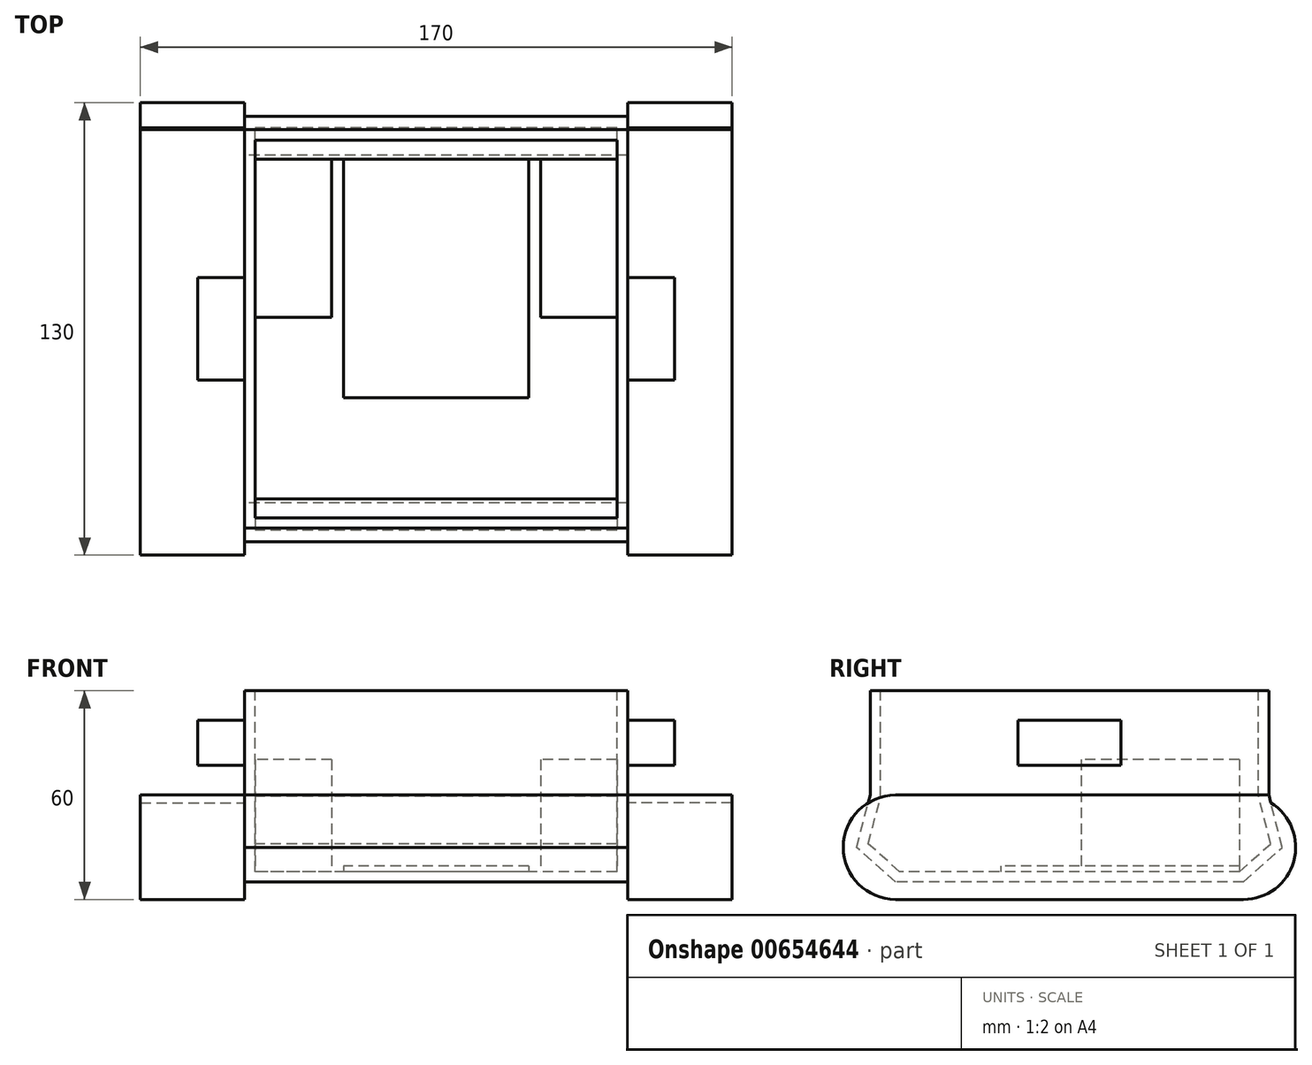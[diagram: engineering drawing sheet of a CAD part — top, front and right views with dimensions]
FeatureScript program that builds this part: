
annotation { "Feature Type Name" : "Feature", "Feature Type Description" : "" }
export const myFeature = defineFeature(function(context is Context, id is Id, definition is map)
    precondition{}
    {
        {
            var Q0;
            Q0=qCreatedBy(makeId("Right.planeOp"),FACE);
            var sketch = newSketch(context, id + "F0", { "sketchPlane" : qUnion([Q0])});
            skLineSegment(sketch, "E0", {"start": v(0, 0) * mm, "end": v(50, 0) * mm, "construction": true});
            skLineSegment(sketch, "E1", {"start": v(0, 0) * mm, "end": v(-50, 0) * mm, "construction": true});
            skCircle(sketch, "E2", {"center": v(50, 0) * mm, "radius": 15 * mm});
            skCircle(sketch, "E3", {"center": v(-50, 0) * mm, "radius": 15 * mm});
            skLineSegment(sketch, "E4", {"start": v(-50, 15) * mm, "end": v(50, 15) * mm});
            skLineSegment(sketch, "E5", {"start": v(50, -15) * mm, "end": v(-50, -15) * mm});
            skLineSegment(sketch, "E6", {"start": v(0, 0) * mm, "end": v(0, -10) * mm, "construction": true});
            skLineSegment(sketch, "E7", {"start": v(0, -10) * mm, "end": v(-50, -10) * mm});
            skLineSegment(sketch, "E8", {"start": v(-50, -10) * mm, "end": v(-61.18, 0) * mm});
            skLineSegment(sketch, "E9", {"start": v(0, -10) * mm, "end": v(50, -10) * mm});
            skLineSegment(sketch, "E10", {"start": v(50, -10) * mm, "end": v(61.18, 0) * mm});
            skLineSegment(sketch, "E11", {"start": v(61.18, 0) * mm, "end": v(57.28, 15) * mm});
            skLineSegment(sketch, "E12", {"start": v(-61.18, 0) * mm, "end": v(-57.28, 15) * mm});
            skLineSegment(sketch, "E13", {"start": v(-57.28, 15) * mm, "end": v(-50, 15) * mm});
            skLineSegment(sketch, "E14", {"start": v(57.28, 15) * mm, "end": v(50, 15) * mm});
            skLineSegment(sketch, "E15.bottom", {"start": v(-57.28, 15) * mm, "end": v(57.28, 15) * mm});
            skLineSegment(sketch, "E15.top", {"start": v(-57.28, 45) * mm, "end": v(57.28, 45) * mm});
            skLineSegment(sketch, "E15.left", {"start": v(-57.28, 15) * mm, "end": v(-57.28, 45) * mm});
            skLineSegment(sketch, "E15.right", {"start": v(57.28, 15) * mm, "end": v(57.28, 45) * mm});
            skLineSegment(sketch, "E16.bottom", {"start": v(14.75, 23.5) * mm, "end": v(-14.75, 23.5) * mm});
            skLineSegment(sketch, "E16.top", {"start": v(14.75, 36.5) * mm, "end": v(-14.75, 36.5) * mm});
            skLineSegment(sketch, "E16.left", {"start": v(14.75, 23.5) * mm, "end": v(14.75, 36.5) * mm});
            skLineSegment(sketch, "E16.right", {"start": v(-14.75, 23.5) * mm, "end": v(-14.75, 36.5) * mm});
            skPoint(sketch, "E16.middle", {"position": v(0, 30) * mm});
            skPoint(sketch, "E16.middle.positionSnap0", {"position": v(-57.28, 30) * mm});
            skPoint(sketch, "E16.centerSnap0", {"position": v(-57.28, 30) * mm});
            skSolve(sketch);
        }
        {
            var Q0;
            {var subQ5=sQuery(id+"F0.wireOp",EDGE,"E4");Q0=makeQuery(id+"F0.imprint","IMPRINT",FACE,{"disambiguationData":[TD([[makeQuery(id+"F0.imprint","IMPRINT",EDGE,{"derivedFrom":subQ5}),-1.0]])]});}
            var Q1;
            {var subQ4=sQuery(id+"F0.wireOp",EDGE,"E10");Q1=makeQuery(id+"F0.imprint","IMPRINT",FACE,{"disambiguationData":[TD([[makeQuery(id+"F0.imprint","IMPRINT",EDGE,{"derivedFrom":subQ4}),1.0]])]});}
            var Q2;
            {var subQ4=sQuery(id+"F0.wireOp",EDGE,"E8");Q2=makeQuery(id+"F0.imprint","IMPRINT",FACE,{"disambiguationData":[TD([[makeQuery(id+"F0.imprint","IMPRINT",EDGE,{"derivedFrom":subQ4}),-1.0]])]});}
            var Q3;
            {var subQ0=sQuery(id+"F0.wireOp",EDGE,"E13");Q3=makeQuery(id+"F0.imprint","IMPRINT",FACE,{"disambiguationData":[TD([[makeQuery(id+"F0.imprint","IMPRINT",EDGE,{"derivedFrom":subQ0}),-1.0]])]});}
            var Q4;
            {var subQ0=sQuery(id+"F0.wireOp",EDGE,"E14");Q4=makeQuery(id+"F0.imprint","IMPRINT",FACE,{"disambiguationData":[TD([[makeQuery(id+"F0.imprint","IMPRINT",EDGE,{"derivedFrom":subQ0}),1.0]])]});}
            var Q5;
            Q5=makeQuery(id+"F0.imprint","IMPRINT",FACE,{"disambiguationData":[TD([[makeQuery(id+"F0.imprint","IMPRINT",EDGE,{"derivedFrom":sQuery(id+"F0.wireOp",EDGE,"E15.top")}),-1.0]])]});
            var Q6;
            {var subQ0=sQuery(id+"F0.wireOp",EDGE,"E11");var subQ1=sQuery(id+"F0.wireOp",EDGE,"E2");var subQ2=makeQuery(id+"F0.imprint","INTERSECT",VERTEX,{"derivedFrom":[subQ1,subQ0]});Q6=makeQuery(id+"F0.imprint","IMPRINT",FACE,{"disambiguationData":[TD([[makeQuery(id+"F0.imprint","IMPRINT",EDGE,{"disambiguationData":[TD([[subQ2,-1.0]])],"derivedFrom":subQ1}),-1.0]])]});}
            var Q7;
            {var subQ0=sQuery(id+"F0.wireOp",EDGE,"E12");var subQ1=sQuery(id+"F0.wireOp",EDGE,"E3");var subQ2=makeQuery(id+"F0.imprint","INTERSECT",VERTEX,{"derivedFrom":[subQ1,subQ0]});Q7=makeQuery(id+"F0.imprint","IMPRINT",FACE,{"disambiguationData":[TD([[makeQuery(id+"F0.imprint","IMPRINT",EDGE,{"disambiguationData":[TD([[subQ2,1.0]])],"derivedFrom":subQ1}),-1.0]])]});}
            var Q8;
            {var subQ5=sQuery(id+"F0.wireOp",EDGE,"E15.bottom");var subQ6=sQuery(id+"F0.wireOp",EDGE,"E2");var subQ7=makeQuery(id+"F0.imprint","INTERSECT",VERTEX,{"derivedFrom":[subQ6,subQ5]});Q8=makeQuery(id+"F0.imprint","IMPRINT",FACE,{"disambiguationData":[TD([[makeQuery(id+"F0.imprint","IMPRINT",EDGE,{"disambiguationData":[TD([[subQ7,-1.0]])],"derivedFrom":subQ6}),-1.0]])]});}
            var Q9;
            Q9=makeQuery(id+"F0.imprint","IMPRINT",FACE,{"disambiguationData":[TD([[makeQuery(id+"F0.imprint","IMPRINT",EDGE,{"derivedFrom":sQuery(id+"F0.wireOp",EDGE,"E16.bottom")}),-1.0]])]});
            extrude(context, id + "F1", {"entities" : qUnion([Q0, Q1, Q2, Q3, Q4, Q5, Q6, Q7, Q8, Q9]), "depth" : 110 * mm, "offsetDistance" : 25 * mm, "symmetric" : true});
        }
        {
            var Q0;
            {var subQ4=sQuery(id+"F0.wireOp",EDGE,"E8");Q0=makeQuery(id+"F0.imprint","IMPRINT",FACE,{"disambiguationData":[TD([[makeQuery(id+"F0.imprint","IMPRINT",EDGE,{"derivedFrom":subQ4}),-1.0]])]});}
            var Q1;
            {var subQ0=sQuery(id+"F0.wireOp",EDGE,"E8");Q1=makeQuery(id+"F0.imprint","IMPRINT",FACE,{"disambiguationData":[TD([[makeQuery(id+"F0.imprint","IMPRINT",EDGE,{"derivedFrom":subQ0}),1.0]])]});}
            var Q2;
            {var subQ4=sQuery(id+"F0.wireOp",EDGE,"E10");Q2=makeQuery(id+"F0.imprint","IMPRINT",FACE,{"disambiguationData":[TD([[makeQuery(id+"F0.imprint","IMPRINT",EDGE,{"derivedFrom":subQ4}),1.0]])]});}
            var Q3;
            {var subQ5=sQuery(id+"F0.wireOp",EDGE,"E4");Q3=makeQuery(id+"F0.imprint","IMPRINT",FACE,{"disambiguationData":[TD([[makeQuery(id+"F0.imprint","IMPRINT",EDGE,{"derivedFrom":subQ5}),-1.0]])]});}
            var Q4;
            {var subQ0=sQuery(id+"F0.wireOp",EDGE,"E10");Q4=makeQuery(id+"F0.imprint","IMPRINT",FACE,{"disambiguationData":[TD([[makeQuery(id+"F0.imprint","IMPRINT",EDGE,{"derivedFrom":subQ0}),-1.0]])]});}
            var Q5;
            {var subQ5=sQuery(id+"F0.wireOp",EDGE,"E5");Q5=makeQuery(id+"F0.imprint","IMPRINT",FACE,{"disambiguationData":[TD([[makeQuery(id+"F0.imprint","IMPRINT",EDGE,{"derivedFrom":subQ5}),-1.0]])]});}
            var Q6;
            {var subQ5=sQuery(id+"F0.wireOp",EDGE,"E15.bottom");var subQ6=sQuery(id+"F0.wireOp",EDGE,"E2");var subQ7=makeQuery(id+"F0.imprint","INTERSECT",VERTEX,{"derivedFrom":[subQ6,subQ5]});Q6=makeQuery(id+"F0.imprint","IMPRINT",FACE,{"disambiguationData":[TD([[makeQuery(id+"F0.imprint","IMPRINT",EDGE,{"disambiguationData":[TD([[subQ7,-1.0]])],"derivedFrom":subQ6}),-1.0]])]});}
            extrude(context, id + "F2", {"entities" : qUnion([Q0, Q1, Q2, Q3, Q4, Q5, Q6]), "depth" : 85 * mm, "offsetDistance" : 25 * mm, "hasSecondDirection" : true, "secondDirectionOppositeDirection" : false, "secondDirectionDepth" : 55 * mm});
        }
        {
            var Q0;
            {var subQ5=sQuery(id+"F0.wireOp",EDGE,"E4");Q0=makeQuery(id+"F0.imprint","IMPRINT",FACE,{"disambiguationData":[TD([[makeQuery(id+"F0.imprint","IMPRINT",EDGE,{"derivedFrom":subQ5}),-1.0]])]});}
            var Q1;
            {var subQ0=sQuery(id+"F0.wireOp",EDGE,"E8");Q1=makeQuery(id+"F0.imprint","IMPRINT",FACE,{"disambiguationData":[TD([[makeQuery(id+"F0.imprint","IMPRINT",EDGE,{"derivedFrom":subQ0}),1.0]])]});}
            var Q2;
            {var subQ0=sQuery(id+"F0.wireOp",EDGE,"E10");Q2=makeQuery(id+"F0.imprint","IMPRINT",FACE,{"disambiguationData":[TD([[makeQuery(id+"F0.imprint","IMPRINT",EDGE,{"derivedFrom":subQ0}),-1.0]])]});}
            var Q3;
            {var subQ4=sQuery(id+"F0.wireOp",EDGE,"E10");Q3=makeQuery(id+"F0.imprint","IMPRINT",FACE,{"disambiguationData":[TD([[makeQuery(id+"F0.imprint","IMPRINT",EDGE,{"derivedFrom":subQ4}),1.0]])]});}
            var Q4;
            {var subQ5=sQuery(id+"F0.wireOp",EDGE,"E5");Q4=makeQuery(id+"F0.imprint","IMPRINT",FACE,{"disambiguationData":[TD([[makeQuery(id+"F0.imprint","IMPRINT",EDGE,{"derivedFrom":subQ5}),-1.0]])]});}
            var Q5;
            {var subQ4=sQuery(id+"F0.wireOp",EDGE,"E8");Q5=makeQuery(id+"F0.imprint","IMPRINT",FACE,{"disambiguationData":[TD([[makeQuery(id+"F0.imprint","IMPRINT",EDGE,{"derivedFrom":subQ4}),-1.0]])]});}
            var Q6;
            {var subQ5=sQuery(id+"F0.wireOp",EDGE,"E15.bottom");var subQ6=sQuery(id+"F0.wireOp",EDGE,"E2");var subQ7=makeQuery(id+"F0.imprint","INTERSECT",VERTEX,{"derivedFrom":[subQ6,subQ5]});Q6=makeQuery(id+"F0.imprint","IMPRINT",FACE,{"disambiguationData":[TD([[makeQuery(id+"F0.imprint","IMPRINT",EDGE,{"disambiguationData":[TD([[subQ7,-1.0]])],"derivedFrom":subQ6}),-1.0]])]});}
            extrude(context, id + "F3", {"entities" : qUnion([Q0, Q1, Q2, Q3, Q4, Q5, Q6]), "oppositeDirection" : true, "depth" : 85 * mm, "offsetDistance" : 25 * mm, "hasSecondDirection" : true, "secondDirectionOppositeDirection" : true, "secondDirectionDepth" : 55 * mm});
        }
        {
            var Q0;
            Q0=makeQuery(id+"F1.opExtrude","SWEPT_FACE",FACE,{"disambiguationData":[OSD([sQuery(id+"F0.wireOp",EDGE,"E15.top")])]});
            shell(context, id + "F4", {"entities" : qUnion([Q0]), "thickness" : 3 * mm});
        }
        {
            var Q0;
            Q0=makeQuery(id+"F4.opShell","OFFSET_FACE",FACE,{"disambiguationData":[OSD([sQuery(id+"F0.wireOp",EDGE,"E7"),sQuery(id+"F0.wireOp",EDGE,"E9")])]});
            var sketch = newSketch(context, id + "F5", { "sketchPlane" : qUnion([Q0])});
            skLineSegment(sketch, "E17", {"start": v(-52, 48.85) * mm, "end": v(-30, 48.85) * mm});
            skLineSegment(sketch, "E18", {"start": v(-30, 48.85) * mm, "end": v(-30, 3.35) * mm});
            skLineSegment(sketch, "E19", {"start": v(-30, 3.35) * mm, "end": v(-52, 3.35) * mm});
            skLineSegment(sketch, "E20", {"start": v(-52, 3.35) * mm, "end": v(-52, 48.85) * mm});
            skLineSegment(sketch, "E21", {"start": v(52, 48.85) * mm, "end": v(30, 48.85) * mm});
            skLineSegment(sketch, "E22", {"start": v(30, 48.85) * mm, "end": v(30, 3.35) * mm});
            skLineSegment(sketch, "E23", {"start": v(30, 3.35) * mm, "end": v(52, 3.35) * mm});
            skLineSegment(sketch, "E24", {"start": v(52, 3.35) * mm, "end": v(52, 48.85) * mm});
            skLineSegment(sketch, "E25", {"start": v(0, 48.85) * mm, "end": v(-26.65, 48.85) * mm});
            skLineSegment(sketch, "E26", {"start": v(0, 48.85) * mm, "end": v(26.65, 48.85) * mm});
            skLineSegment(sketch, "E27", {"start": v(26.65, 48.85) * mm, "end": v(26.65, -19.75) * mm});
            skLineSegment(sketch, "E28", {"start": v(-26.65, 48.85) * mm, "end": v(-26.65, -19.75) * mm});
            skLineSegment(sketch, "E29", {"start": v(-26.65, -19.75) * mm, "end": v(26.65, -19.75) * mm});
            skSolve(sketch);
        }
        {
            var Q0;
            Q0=makeQuery(id+"F5.imprint","IMPRINT",FACE,{"disambiguationData":[TD([[makeQuery(id+"F5.imprint","IMPRINT",EDGE,{"derivedFrom":sQuery(id+"F5.wireOp",EDGE,"E17")}),1.0]])]});
            var Q1;
            Q1=makeQuery(id+"F5.imprint","IMPRINT",FACE,{"disambiguationData":[TD([[makeQuery(id+"F5.imprint","IMPRINT",EDGE,{"derivedFrom":sQuery(id+"F5.wireOp",EDGE,"E21")}),1.0]])]});
            extrude(context, id + "F6", {"entities" : qUnion([Q0, Q1]), "depth" : 32.2 * mm, "offsetDistance" : 25 * mm});
        }
        {
            var Q0;
            Q0=makeQuery(id+"F5.imprint","IMPRINT",FACE,{"disambiguationData":[TD([[makeQuery(id+"F5.imprint","IMPRINT",EDGE,{"derivedFrom":sQuery(id+"F5.wireOp",EDGE,"E25")}),1.0]])]});
            extrude(context, id + "F7", {"entities" : qUnion([Q0]), "depth" : 1.6 * mm, "offsetDistance" : 25 * mm});
        }
        {
            var Q0;
            Q0=makeQuery(id+"F0.imprint","IMPRINT",FACE,{"disambiguationData":[TD([[makeQuery(id+"F0.imprint","IMPRINT",EDGE,{"derivedFrom":sQuery(id+"F0.wireOp",EDGE,"E16.bottom")}),-1.0]])]});
            extrude(context, id + "F8", {"entities" : qUnion([Q0]), "depth" : 68.5 * mm, "offsetDistance" : 25 * mm, "hasSecondDirection" : true, "secondDirectionOppositeDirection" : false, "secondDirectionDepth" : 55 * mm});
        }
        {
            var Q0;
            Q0=makeQuery(id+"F0.imprint","IMPRINT",FACE,{"disambiguationData":[TD([[makeQuery(id+"F0.imprint","IMPRINT",EDGE,{"derivedFrom":sQuery(id+"F0.wireOp",EDGE,"E16.bottom")}),-1.0]])]});
            extrude(context, id + "F9", {"entities" : qUnion([Q0]), "oppositeDirection" : true, "depth" : 68.5 * mm, "offsetDistance" : 25 * mm, "hasSecondDirection" : true, "secondDirectionOppositeDirection" : true, "secondDirectionDepth" : 55 * mm});
        }
    });
